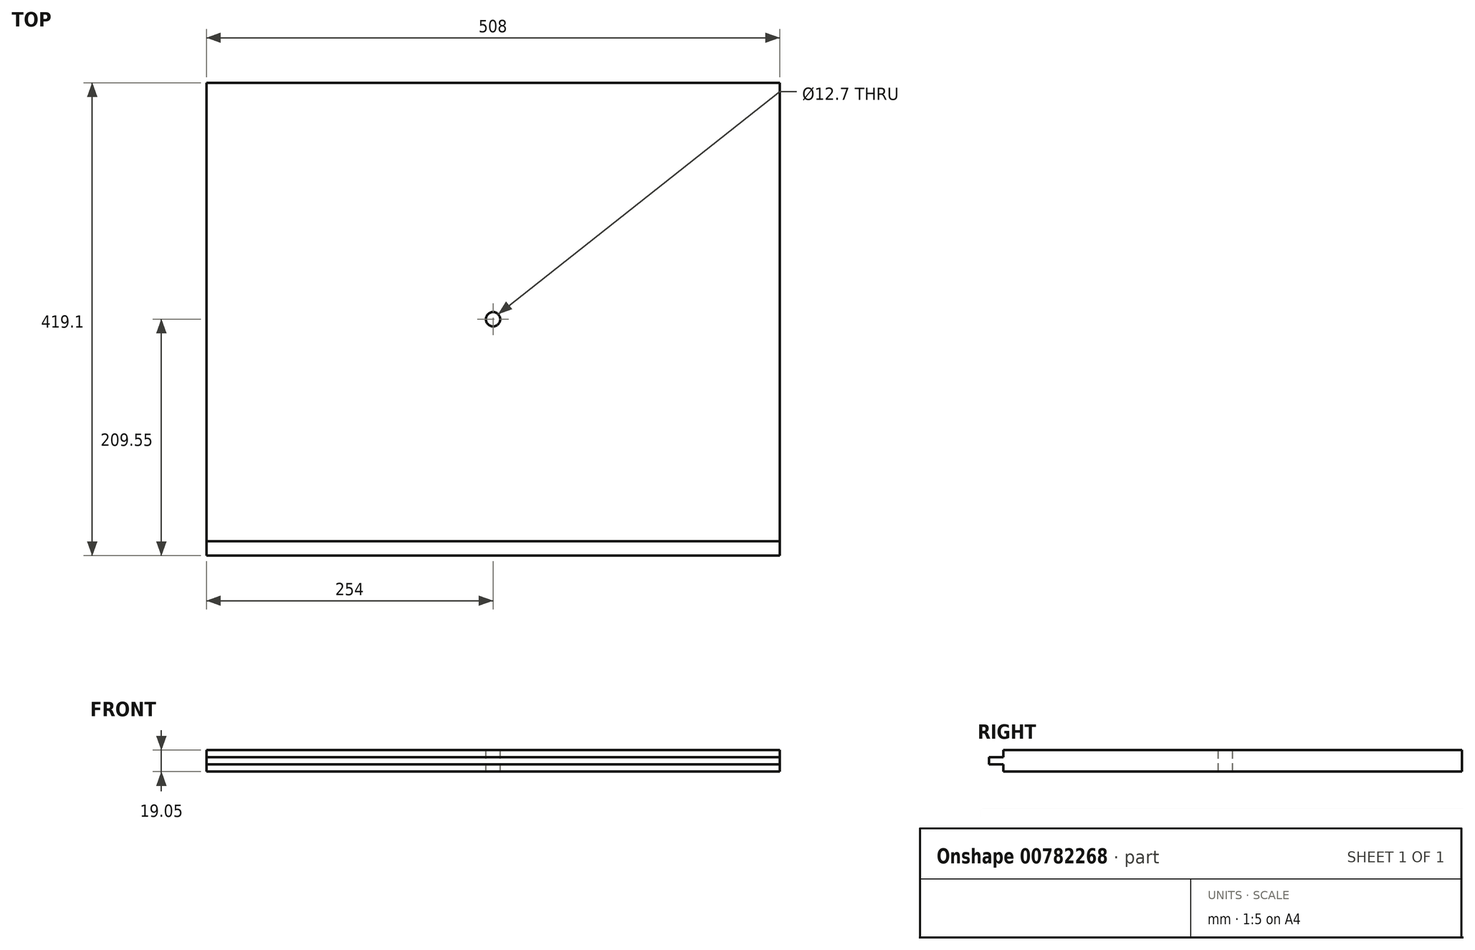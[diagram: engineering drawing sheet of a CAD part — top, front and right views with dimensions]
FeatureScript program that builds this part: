
annotation { "Feature Type Name" : "Feature", "Feature Type Description" : "" }
export const myFeature = defineFeature(function(context is Context, id is Id, definition is map)
    precondition{}
    {
        {
            var Q0;
            Q0=qCreatedBy(makeId("Top.planeOp"),FACE);
            var sketch = newSketch(context, id + "F0", { "sketchPlane" : qUnion([Q0])});
            skLineSegment(sketch, "E0.bottom", {"start": v(-254, 209.55) * mm, "end": v(254, 209.55) * mm});
            skLineSegment(sketch, "E0.top", {"start": v(-254, -209.55) * mm, "end": v(254, -209.55) * mm});
            skLineSegment(sketch, "E0.left", {"start": v(-254, 209.55) * mm, "end": v(-254, -209.55) * mm});
            skLineSegment(sketch, "E0.right", {"start": v(254, 209.55) * mm, "end": v(254, -209.55) * mm});
            skLineSegment(sketch, "E1", {"start": v(-254, -209.55) * mm, "end": v(254, 209.55) * mm, "construction": true});
            skSolve(sketch);
        }
        {
            var Q0;
            Q0=makeQuery(id+"F0.imprint","IMPRINT",FACE,{"disambiguationData":[TD([[makeQuery(id+"F0.imprint","IMPRINT",EDGE,{"derivedFrom":sQuery(id+"F0.wireOp",EDGE,"E0.bottom")}),-1.0]])]});
            extrude(context, id + "F1", {"entities" : qUnion([Q0]), "depth" : 19.05 * mm, "offsetDistance" : 25.4 * mm});
        }
        {
            var Q0;
            Q0=makeQuery(id+"F1.opExtrude","SWEPT_FACE",FACE,{"disambiguationData":[OSD([sQuery(id+"F0.wireOp",EDGE,"E0.top")])]});
            var sketch = newSketch(context, id + "F2", { "sketchPlane" : qUnion([Q0])});
            skLineSegment(sketch, "E2.0", {"start": v(-254, 0) * mm, "end": v(254, 0) * mm});
            skLineSegment(sketch, "E3", {"start": v(-254, 9.52) * mm, "end": v(254, 9.53) * mm, "construction": true});
            skLineSegment(sketch, "E4.0", {"start": v(-254, 6.35) * mm, "end": v(254, 6.35) * mm});
            skLineSegment(sketch, "E5.0", {"start": v(254, 6.35) * mm, "end": v(254, 0) * mm});
            skPoint(sketch, "E6.orphan", {"position": v(254, 19.05) * mm});
            skLineSegment(sketch, "E7.0", {"start": v(-254, 6.35) * mm, "end": v(-254, 0) * mm});
            skPoint(sketch, "E8.orphan", {"position": v(-254, 19.05) * mm});
            skLineSegment(sketch, "E9.MirrorCS", {"start": v(-254, 12.7) * mm, "end": v(254, 12.7) * mm});
            skLineSegment(sketch, "E10.MirrorCS", {"start": v(-254, 12.7) * mm, "end": v(-254, 19.05) * mm});
            skLineSegment(sketch, "E11.MirrorCS", {"start": v(-254, 19.05) * mm, "end": v(254, 19.05) * mm});
            skLineSegment(sketch, "E12.MirrorCS", {"start": v(254, 12.7) * mm, "end": v(254, 19.05) * mm});
            skSolve(sketch);
        }
        {
            var Q0;
            Q0 = qSketchRegion(id + "F2", true);
            extrude(context, id + "F3", {"entities" : qUnion([Q0]), "operationType" : NewBodyOperationType.REMOVE, "oppositeDirection" : true, "depth" : 12.7 * mm, "offsetDistance" : 25.4 * mm});
        }
        {
            var Q0;
            Q0=makeQuery(id+"F1.opExtrude","CAP_FACE",FACE,{"disambiguationData":[OSD([sQuery(id+"F0.wireOp",EDGE,"E0.bottom"),sQuery(id+"F0.wireOp",EDGE,"E0.top"),sQuery(id+"F0.wireOp",EDGE,"E0.left"),sQuery(id+"F0.wireOp",EDGE,"E0.right")])],"isStart":false});
            var sketch = newSketch(context, id + "F4", { "sketchPlane" : qUnion([Q0])});
            skCircle(sketch, "E13", {"center": v(0, 0) * mm, "radius": 6.35 * mm});
            skSolve(sketch);
        }
        {
            var Q0;
            Q0 = qSketchRegion(id + "F4", true);
            extrude(context, id + "F5", {"entities" : qUnion([Q0]), "operationType" : NewBodyOperationType.REMOVE, "endBound" : BoundingType.THROUGH_ALL, "oppositeDirection" : true, "depth" : 25.4 * mm, "offsetDistance" : 25.4 * mm});
        }
    });
